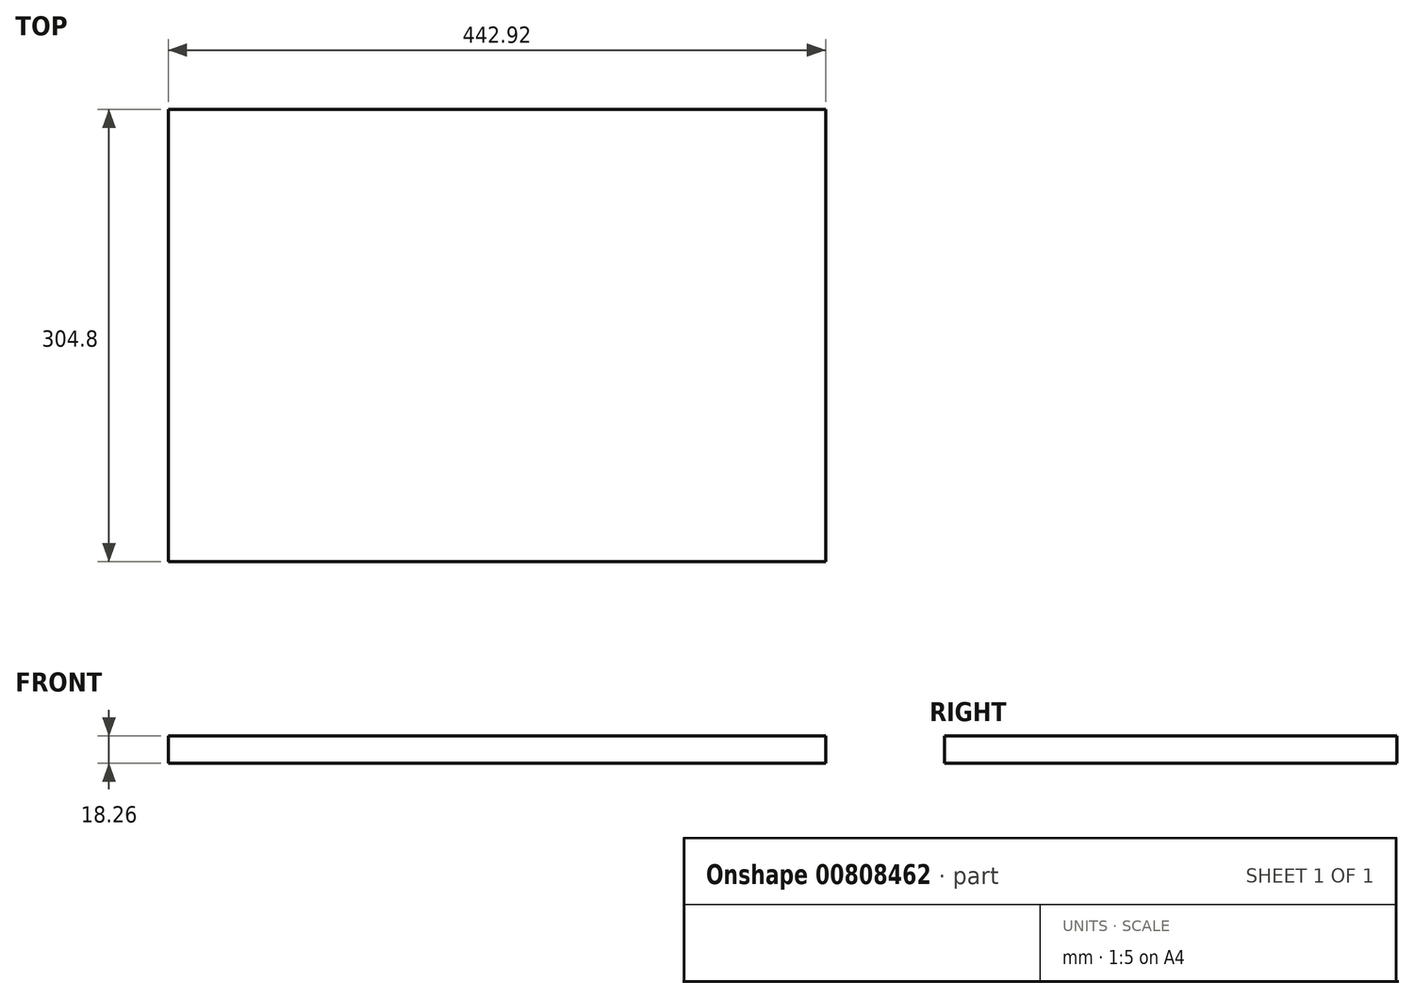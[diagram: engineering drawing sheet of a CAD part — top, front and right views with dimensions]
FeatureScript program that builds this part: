
annotation { "Feature Type Name" : "Feature", "Feature Type Description" : "" }
export const myFeature = defineFeature(function(context is Context, id is Id, definition is map)
    precondition{}
    {
        {
            var Q0;
            Q0=qCreatedBy(makeId("Top.planeOp"),FACE);
            var sketch = newSketch(context, id + "F0", { "sketchPlane" : qUnion([Q0])});
            skLineSegment(sketch, "E0.bottom", {"start": v(221.46, 152.4) * mm, "end": v(-221.46, 152.4) * mm});
            skLineSegment(sketch, "E0.top", {"start": v(221.46, -152.4) * mm, "end": v(-221.46, -152.4) * mm});
            skLineSegment(sketch, "E0.left", {"start": v(221.46, 152.4) * mm, "end": v(221.46, -152.4) * mm});
            skLineSegment(sketch, "E0.right", {"start": v(-221.46, 152.4) * mm, "end": v(-221.46, -152.4) * mm});
            skPoint(sketch, "E0.middle", {"position": v(0, 0) * mm});
            skSolve(sketch);
        }
        {
            var Q0;
            Q0=makeQuery(id+"F0.imprint","IMPRINT",FACE,{"disambiguationData":[TD([[makeQuery(id+"F0.imprint","IMPRINT",EDGE,{"derivedFrom":sQuery(id+"F0.wireOp",EDGE,"E0.bottom")}),1.0]])]});
            extrude(context, id + "F1", {"entities" : qUnion([Q0]), "depth" : 18.26 * mm, "offsetDistance" : 25.4 * mm});
        }
    });
